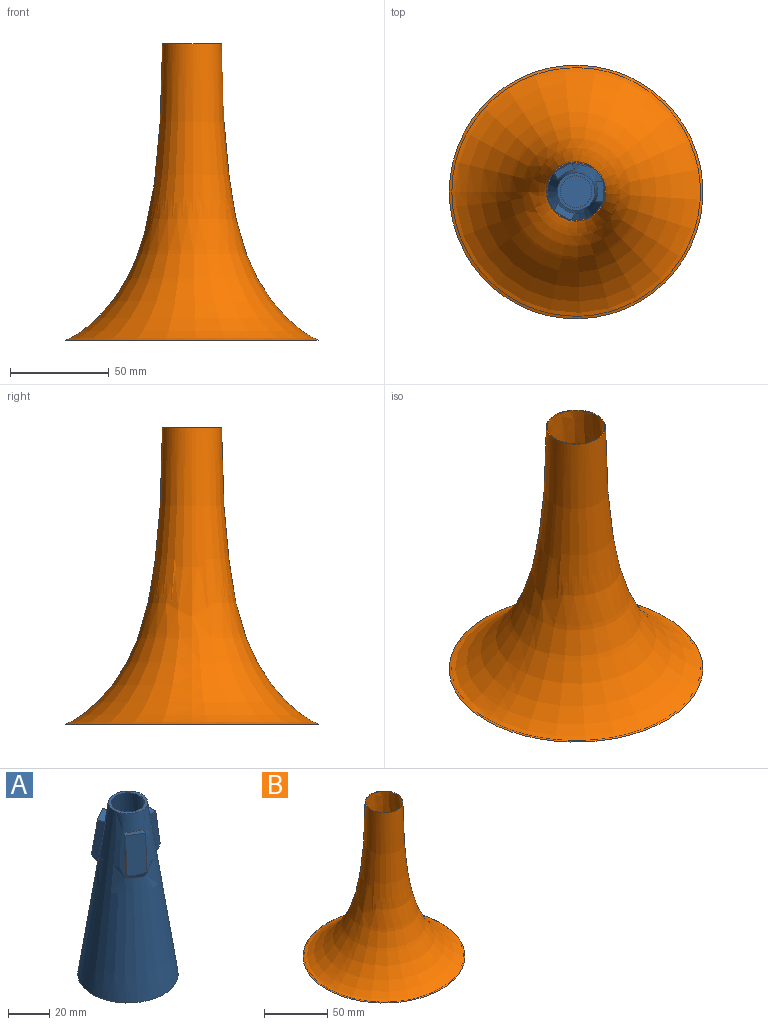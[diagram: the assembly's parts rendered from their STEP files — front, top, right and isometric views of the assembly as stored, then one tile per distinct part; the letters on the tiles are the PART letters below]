
ASSEMBLY  parts=2 mates=1
PART A: 20 faces, bbox 50.4x50.4x103.4 mm
  f0: cone r=24.23mm half-angle=8.3deg, axis (0,0,-1), area 10092.6mm2, adj f2,f3,f5,f7,f8,f9,f10,f11
  f1: plane 45x45mm, normal (0,0,1), area 1590.4mm2, adj f4
  f2: plane 48.47x48.47mm, normal (0,0,-1), area 1844.9mm2, adj f0
  f3: plane 19.03x19.03mm, normal (0,0,1), area 83.4mm2, adj f0,f4
  f4: cone r=22.5mm half-angle=8.3deg, axis (0,0,-1), area 9682.1mm2, adj f1,f3
  f5: plane 10.35x4.5mm, normal (-0.14,0,0.99), area 33.9mm2, adj f0,f6,f7,f8
  f6: plane 23.67x11.95mm, normal (0.99,0,0.14), area 217.2mm2, adj f5,f7,f8,f9
  f7: plane 25.57x7.48mm, normal (0,1,0), area 93.2mm2, adj f0,f5,f6,f9
  f8: plane 25.57x7.48mm, normal (0,-1,0), area 93.2mm2, adj f0,f5,f6,f9
  f9: bspline ~12.51x4.35mm, area 53.6mm2, adj f0,f6,f7,f8
  f10: plane 25.57x6.51mm, normal (0.87,0.5,0), area 93.2mm2, adj f0,f11,f13,f14
  f11: plane 11.08x8.94mm, normal (0.07,-0.12,0.99), area 33.9mm2, adj f0,f10,f12,f13
  f12: plane 25.57x6.51mm, normal (-0.87,-0.5,0), area 93.2mm2, adj f0,f11,f13,f14
  f13: plane 23.67x12.13mm, normal (-0.49,0.86,0.14), area 217.2mm2, adj f10,f11,f12,f14
  f14: bspline ~11.2x8.14mm, area 53.6mm2, adj f0,f10,f12,f13
  f15: plane 25.57x6.51mm, normal (-0.87,0.5,0), area 93.2mm2, adj f0,f16,f18,f19
  f16: plane 11.08x8.94mm, normal (0.07,0.12,0.99), area 33.9mm2, adj f0,f15,f17,f18
  f17: plane 25.57x6.51mm, normal (0.87,-0.5,0), area 93.2mm2, adj f0,f16,f18,f19
  f18: plane 23.67x12.13mm, normal (-0.49,-0.86,0.14), area 217.2mm2, adj f15,f16,f17,f19
  f19: bspline ~11.2x8.14mm, area 53.6mm2, adj f0,f15,f17,f18
PART B: 4 faces, bbox 128.5x128.5x150 mm
  f0: cone r=14.6mm half-angle=87.2deg, axis (0,0,1), area 37.2mm2, adj f1,f3
  f1: revolved ~149.98x125.94mm, area 27616.5mm2, adj f0,f2
  f2: plane 128.5x128.5mm, normal (0,0,-1), area 512.1mm2, adj f1,f3
  f3: revolved ~150x128.5mm, area 28357mm2, adj f0,f2
PLACE A t=(-92.62,10.78,187.96)mm
PLACE B t=(-92.62,10.78,183.53)mm
MATE slider B.f0 <-> A.f0  axis (0,0,-1) through (-92.62,10.78,183.04)mm
